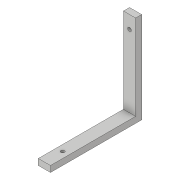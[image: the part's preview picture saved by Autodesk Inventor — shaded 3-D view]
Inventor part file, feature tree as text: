
AUTODESK INVENTOR PART (.ipt)
format: ipt  version: 2019 (Build 230136000, 136)  size: 99,328 bytes
history: native  units: in
note: dims shown in document units (in); Inventor stores cm internally (conversion verified against a paired STEP export)
features: sketch x5, extrude x4
ambient origin geometry x8: Origin, YZ Plane, XZ Plane, XY Plane, X Axis, Y Axis, Z Axis, Center Point
bodies: Solid1 (feature_tree)
feature tree (9):
  extrude  "Extrusion1"  Depth=0.2953in
  sketch  "Sketch2"  dims[d2=0.0197in d3=0.0in d4=0.0394in]
  extrude  "Extrusion2"  Depth=0.0394in
  extrude  "Extrusion3"  Depth=0.0197in TaperAngle=0.0deg
  extrude  "Extrusion4"  Depth=0.0197in
  sketch  "Sketch1"  dims[d0=0.0394in d1=0.2953in]
  sketch  "Sketch3"  dims[d5=0.2953in d6=0.0197in d7=0.0in]
  sketch  "Sketch4"  dims[d8=0.0591in d9=0.0197in]
  sketch  "Sketch5"  dims[d10=0.0118in d11=0.0in d12=0.0in d13=0.0591in d14=0.0197in d15=0.0118in d16=0.0197in d17=0.0in]
